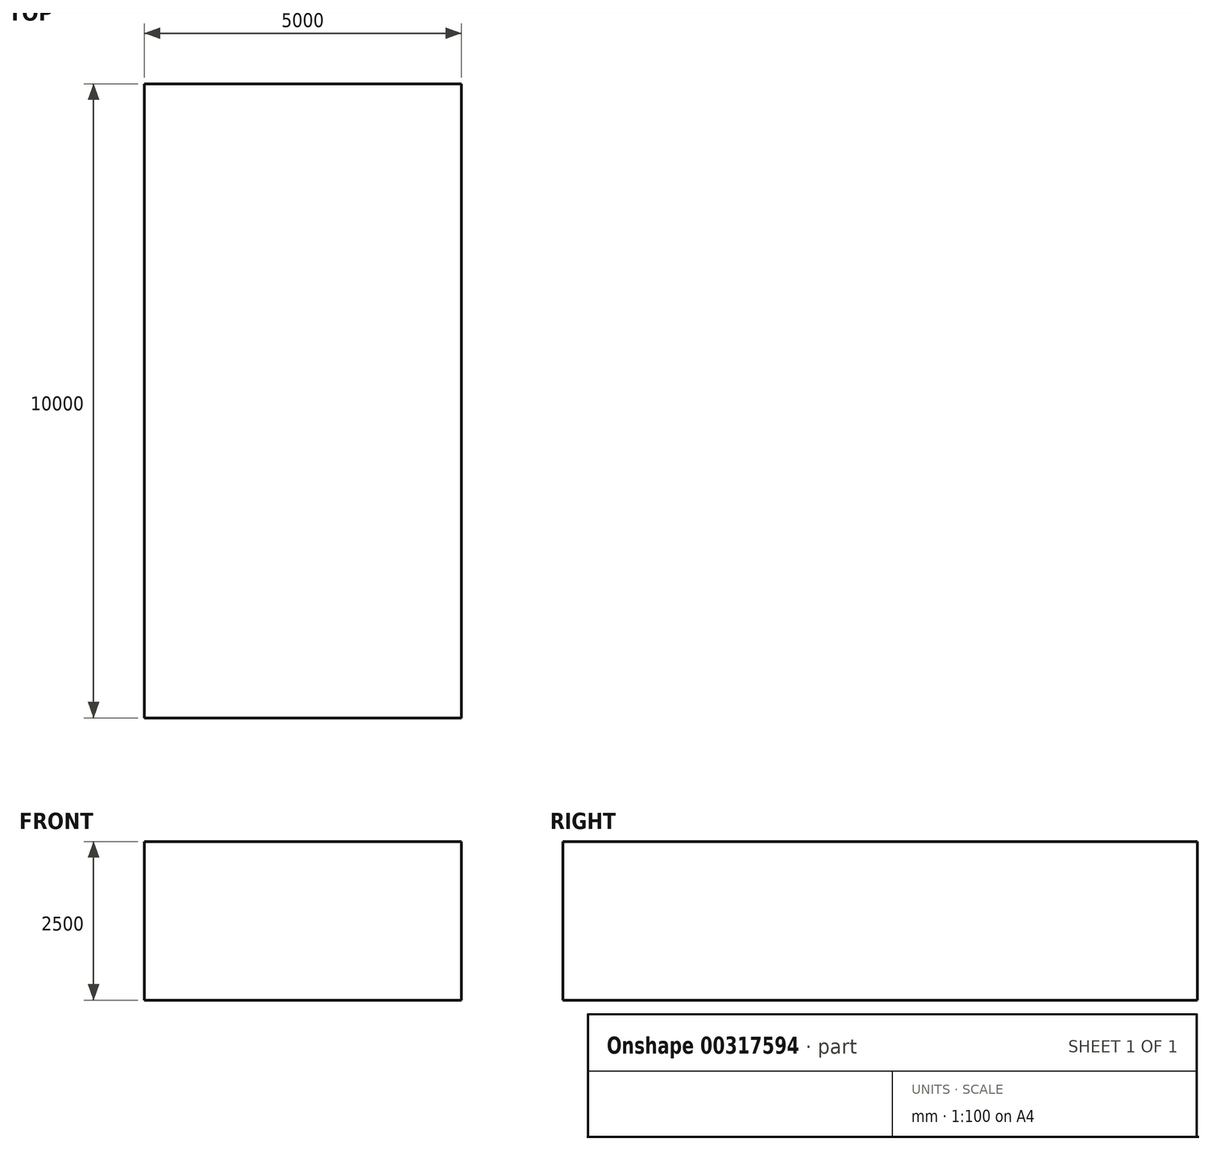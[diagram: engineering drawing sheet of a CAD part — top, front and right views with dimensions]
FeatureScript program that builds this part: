
annotation { "Feature Type Name" : "Feature", "Feature Type Description" : "" }
export const myFeature = defineFeature(function(context is Context, id is Id, definition is map)
    precondition{}
    {
        {
            var Q0;
            Q0=qCreatedBy(makeId("Front.planeOp"),FACE);
            var sketch = newSketch(context, id + "F0", { "sketchPlane" : qUnion([Q0])});
            skLineSegment(sketch, "E0.bottom", {"start": v(0, 0) * mm, "end": v(5000, 0) * mm});
            skLineSegment(sketch, "E0.top", {"start": v(0, 2500) * mm, "end": v(5000, 2500) * mm});
            skLineSegment(sketch, "E0.left", {"start": v(0, 0) * mm, "end": v(0, 2500) * mm});
            skLineSegment(sketch, "E0.right", {"start": v(5000, 0) * mm, "end": v(5000, 2500) * mm});
            skSolve(sketch);
        }
        {
            var Q0;
            Q0=makeQuery(id+"F0.imprint","IMPRINT",FACE,{"disambiguationData":[TD([[makeQuery(id+"F0.imprint","IMPRINT",EDGE,{"derivedFrom":sQuery(id+"F0.wireOp",EDGE,"E0.bottom")}),1.0]])]});
            extrude(context, id + "F1", {"entities" : qUnion([Q0]), "depth" : 10000 * mm});
        }
    });
